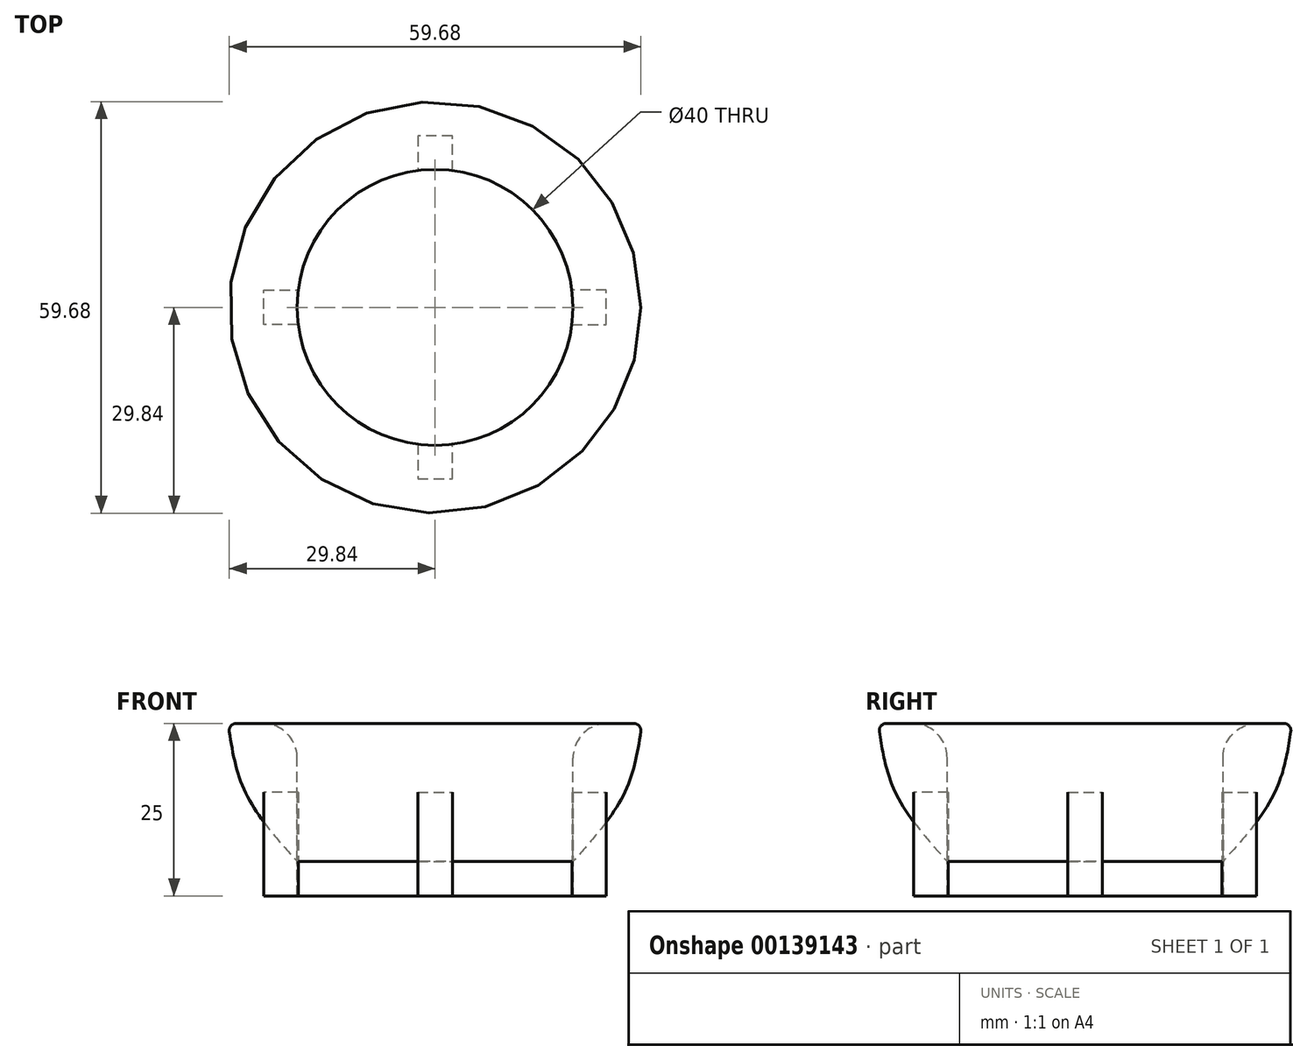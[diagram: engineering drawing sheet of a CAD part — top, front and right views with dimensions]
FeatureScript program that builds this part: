
annotation { "Feature Type Name" : "Feature", "Feature Type Description" : "" }
export const myFeature = defineFeature(function(context is Context, id is Id, definition is map)
    precondition{}
    {
        {
            var Q0;
            Q0=qCreatedBy(makeId("Front.planeOp"),FACE);
            var sketch = newSketch(context, id + "F0", { "sketchPlane" : qUnion([Q0])});
            skLineSegment(sketch, "E0", {"start": v(0, 0) * mm, "end": v(-20, 0) * mm});
            skLineSegment(sketch, "E1", {"start": v(-20, 0) * mm, "end": v(-20, 10) * mm});
            skLineSegment(sketch, "E2", {"start": v(-20, 10) * mm, "end": v(0, 10) * mm});
            skLineSegment(sketch, "E3", {"start": v(0, 10) * mm, "end": v(0, 0) * mm});
            skLineSegment(sketch, "E4", {"start": v(0, 10) * mm, "end": v(0, 30) * mm});
            skLineSegment(sketch, "E5", {"start": v(-20, 30) * mm, "end": v(-30, 30) * mm});
            skLineSegment(sketch, "E6", {"start": v(-20, 30) * mm, "end": v(-20, 10) * mm});
            skPoint(sketch, "E7.positionSnap1", {"position": v(-20, 20) * mm});
            skLineSegment(sketch, "E8", {"start": v(-30, 30) * mm, "end": v(-25, 30) * mm});
            skPoint(sketch, "E9", {"position": v(-27.5, 20) * mm});
            skFitSpline(sketch, "E10", {"points": [v(-30, 30) * mm, v(-27.5, 20) * mm, v(-20, 10) * mm], "startDerivative": vector(3.1, -21.47) * mm, "endDerivative": vector(16.68, -18.57) * mm});
            skSolve(sketch);
        }
        {
            var Q0;
            Q0=makeQuery(id+"F0.imprint","IMPRINT",FACE,{"disambiguationData":[TD([[makeQuery(id+"F0.imprint","IMPRINT",EDGE,{"derivedFrom":sQuery(id+"F0.wireOp",EDGE,"E5")}),1.0]])]});
            var Q1;
            Q1=makeQuery(id+"F0.imprint","IMPRINT",FACE,{"disambiguationData":[TD([[makeQuery(id+"F0.imprint","IMPRINT",EDGE,{"derivedFrom":sQuery(id+"F0.wireOp",EDGE,"E0")}),-1.0]])]});
            var Q2;
            Q2=sQuery(id+"F0.wireOp",EDGE,"E3");
            revolve(context, id + "F1", {"entities" : qUnion([Q0, Q1]), "axis" : qUnion([Q2]), "revolveType" : RevolveType.FULL});
        }
        {
            var Q0;
            Q0=makeQuery(id+"F1.opRevolve","SWEPT_EDGE",EDGE,{"disambiguationData":[OSD([sQuery(id+"F0.wireOp",EDGE,"E5"),sQuery(id+"F0.wireOp",EDGE,"E6")])]});
            fillet(context, id + "F2", {"entities" : qUnion([Q0]), "radius" : 5 * mm, "tangentPropagation" : true, "allowEdgeOverflow" : false});
        }
        {
            var Q0;
            Q0=makeQuery(id+"F1.opRevolve","SWEPT_FACE",FACE,{"disambiguationData":[OSD([sQuery(id+"F0.wireOp",EDGE,"E0")])]});
            var sketch = newSketch(context, id + "F3", { "sketchPlane" : qUnion([Q0])});
            skLineSegment(sketch, "E11", {"start": v(0, 0) * mm, "end": v(-2.5, 0) * mm});
            skLineSegment(sketch, "E12", {"start": v(0, 0) * mm, "end": v(2.5, 0) * mm});
            skLineSegment(sketch, "E13", {"start": v(0, 0) * mm, "end": v(0, 2.5) * mm});
            skLineSegment(sketch, "E14", {"start": v(0, 0) * mm, "end": v(0, -2.5) * mm});
            skLineSegment(sketch, "E15", {"start": v(-2.5, 0) * mm, "end": v(-2.5, 19.84) * mm});
            skLineSegment(sketch, "E16", {"start": v(2.5, 0) * mm, "end": v(2.5, 19.84) * mm});
            skLineSegment(sketch, "E17", {"start": v(0, 2.5) * mm, "end": v(19.84, 2.5) * mm});
            skLineSegment(sketch, "E18", {"start": v(0, -2.5) * mm, "end": v(19.84, -2.5) * mm});
            skLineSegment(sketch, "E19", {"start": v(-2.5, 0) * mm, "end": v(-2.5, -19.84) * mm});
            skLineSegment(sketch, "E20", {"start": v(0, 2.5) * mm, "end": v(-19.84, 2.5) * mm});
            skLineSegment(sketch, "E21", {"start": v(0, -2.5) * mm, "end": v(-19.84, -2.5) * mm});
            skLineSegment(sketch, "E22", {"start": v(-2.5, 19.84) * mm, "end": v(-2.5, 24.84) * mm});
            skLineSegment(sketch, "E23", {"start": v(-2.5, 24.84) * mm, "end": v(2.5, 24.84) * mm});
            skLineSegment(sketch, "E24", {"start": v(2.5, 24.84) * mm, "end": v(2.5, 19.84) * mm});
            skLineSegment(sketch, "E25", {"start": v(19.84, 2.5) * mm, "end": v(24.84, 2.5) * mm});
            skLineSegment(sketch, "E26", {"start": v(24.84, 2.5) * mm, "end": v(24.84, -2.5) * mm});
            skLineSegment(sketch, "E27", {"start": v(24.84, -2.5) * mm, "end": v(19.84, -2.5) * mm});
            skLineSegment(sketch, "E28", {"start": v(2.5, 0) * mm, "end": v(2.5, -19.84) * mm});
            skLineSegment(sketch, "E29", {"start": v(2.5, -19.84) * mm, "end": v(2.5, -24.84) * mm});
            skLineSegment(sketch, "E30", {"start": v(2.5, -24.84) * mm, "end": v(-2.5, -24.84) * mm});
            skLineSegment(sketch, "E31", {"start": v(-2.5, -24.84) * mm, "end": v(-2.5, -19.84) * mm});
            skLineSegment(sketch, "E32", {"start": v(-19.84, 2.5) * mm, "end": v(-24.84, 2.5) * mm});
            skLineSegment(sketch, "E33", {"start": v(-24.84, 2.5) * mm, "end": v(-24.84, -2.5) * mm});
            skLineSegment(sketch, "E34", {"start": v(-24.84, -2.5) * mm, "end": v(-19.84, -2.5) * mm});
            skSolve(sketch);
        }
        {
            var Q0;
            {var subQ0=sQuery(id+"F3.wireOp",EDGE,"E25");Q0=makeQuery(id+"F3.imprint","IMPRINT",FACE,{"disambiguationData":[TD([[makeQuery(id+"F3.imprint","IMPRINT",EDGE,{"derivedFrom":subQ0}),-1.0]])]});}
            var Q1;
            {var subQ0=sQuery(id+"F3.wireOp",EDGE,"E29");Q1=makeQuery(id+"F3.imprint","IMPRINT",FACE,{"disambiguationData":[TD([[makeQuery(id+"F3.imprint","IMPRINT",EDGE,{"derivedFrom":subQ0}),-1.0]])]});}
            var Q2;
            {var subQ0=sQuery(id+"F3.wireOp",EDGE,"E22");Q2=makeQuery(id+"F3.imprint","IMPRINT",FACE,{"disambiguationData":[TD([[makeQuery(id+"F3.imprint","IMPRINT",EDGE,{"derivedFrom":subQ0}),-1.0]])]});}
            var Q3;
            {var subQ0=sQuery(id+"F3.wireOp",EDGE,"E32");Q3=makeQuery(id+"F3.imprint","IMPRINT",FACE,{"disambiguationData":[TD([[makeQuery(id+"F3.imprint","IMPRINT",EDGE,{"derivedFrom":subQ0}),1.0]])]});}
            extrude(context, id + "F4", {"entities" : qUnion([Q0, Q1, Q2, Q3]), "oppositeDirection" : true, "depth" : 20 * mm});
        }
        {
            var Q0;
            Q0=makeQuery(id+"F1.opRevolve","SWEPT_EDGE",EDGE,{"disambiguationData":[OSD([sQuery(id+"F0.wireOp",EDGE,"E8"),sQuery(id+"F0.wireOp",EDGE,"E10")])]});
            fillet(context, id + "F5", {"entities" : qUnion([Q0]), "radius" : 1 * mm, "tangentPropagation" : true, "allowEdgeOverflow" : false});
        }
        {
            var Q0;
            Q0=makeQuery(id+"F1.opRevolve","SWEPT_FACE",FACE,{"disambiguationData":[OSD([sQuery(id+"F0.wireOp",EDGE,"E0")])]});
            var Q1;
            Q1=makeQuery(id+"F4.opExtrude","CAP_FACE",FACE,{"disambiguationData":[OSD([sQuery(id+"F0.wireOp",EDGE,"E0"),sQuery(id+"F0.wireOp",EDGE,"E1"),sQuery(id+"F3.wireOp",EDGE,"E22"),sQuery(id+"F3.wireOp",EDGE,"E23"),sQuery(id+"F3.wireOp",EDGE,"E24")])],"isStart":true});
            var Q2;
            Q2=makeQuery(id+"F4.opExtrude","CAP_FACE",FACE,{"disambiguationData":[OSD([sQuery(id+"F0.wireOp",EDGE,"E0"),sQuery(id+"F0.wireOp",EDGE,"E1"),sQuery(id+"F3.wireOp",EDGE,"E32"),sQuery(id+"F3.wireOp",EDGE,"E33"),sQuery(id+"F3.wireOp",EDGE,"E34")])],"isStart":true});
            var Q3;
            Q3=makeQuery(id+"F4.opExtrude","CAP_FACE",FACE,{"disambiguationData":[OSD([sQuery(id+"F0.wireOp",EDGE,"E0"),sQuery(id+"F0.wireOp",EDGE,"E1"),sQuery(id+"F3.wireOp",EDGE,"E29"),sQuery(id+"F3.wireOp",EDGE,"E30"),sQuery(id+"F3.wireOp",EDGE,"E31")])],"isStart":true});
            var Q4;
            Q4=makeQuery(id+"F4.opExtrude","CAP_FACE",FACE,{"disambiguationData":[OSD([sQuery(id+"F0.wireOp",EDGE,"E0"),sQuery(id+"F0.wireOp",EDGE,"E1"),sQuery(id+"F3.wireOp",EDGE,"E25"),sQuery(id+"F3.wireOp",EDGE,"E26"),sQuery(id+"F3.wireOp",EDGE,"E27")])],"isStart":true});
            extrude(context, id + "F6", {"entities" : qUnion([Q0, Q1, Q2, Q3, Q4]), "operationType" : NewBodyOperationType.REMOVE, "oppositeDirection" : true, "depth" : 5 * mm});
        }
    });
